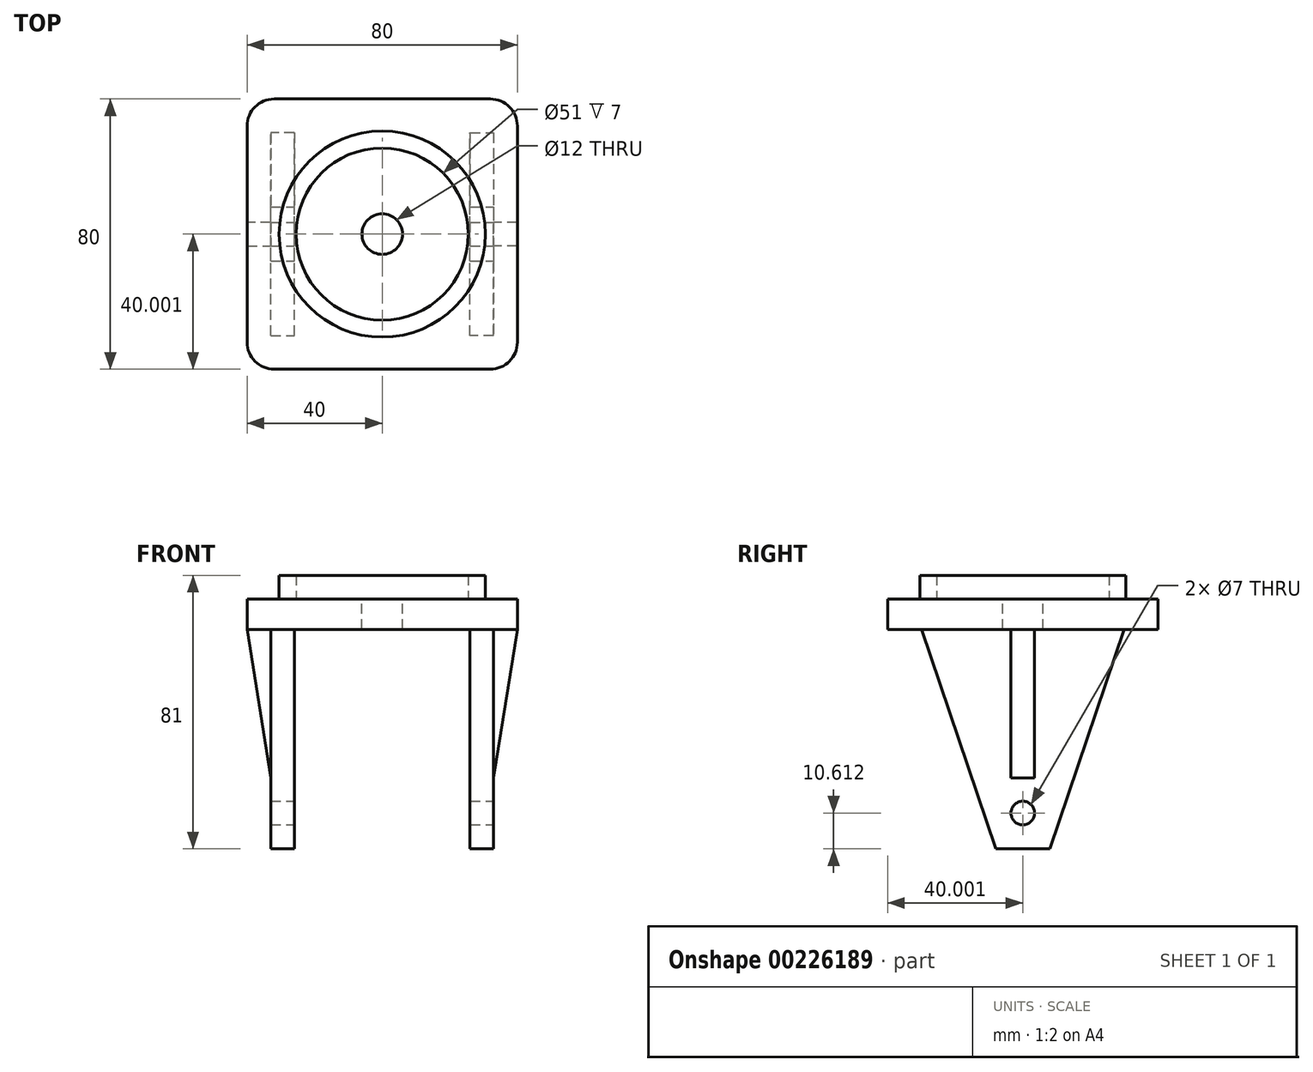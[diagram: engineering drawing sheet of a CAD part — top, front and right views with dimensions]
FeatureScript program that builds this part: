
annotation { "Feature Type Name" : "Feature", "Feature Type Description" : "" }
export const myFeature = defineFeature(function(context is Context, id is Id, definition is map)
    precondition{}
    {
        {
            var Q0;
            Q0=qCreatedBy(makeId("Top.planeOp"),FACE);
            var sketch = newSketch(context, id + "F0", { "sketchPlane" : qUnion([Q0])});
            skLineSegment(sketch, "E0.bottom", {"start": v(-30.4, 30.32) * mm, "end": v(33.6, 30.32) * mm});
            skLineSegment(sketch, "E0.top", {"start": v(-30.4, -49.68) * mm, "end": v(33.6, -49.68) * mm});
            skLineSegment(sketch, "E0.left", {"start": v(-38.4, 22.32) * mm, "end": v(-38.4, -41.68) * mm});
            skLineSegment(sketch, "E0.right", {"start": v(41.6, 22.32) * mm, "end": v(41.6, -41.68) * mm});
            skPoint(sketch, "E1.visualSharp", {"position": v(-38.4, 30.32) * mm});
            skArc(sketch, "E1.filletArc", {"start": v(-30.4, 30.32) * mm, "mid": v(-36.05, 27.98) * mm, "end": v(-38.4, 22.32) * mm});
            skPoint(sketch, "E2.visualSharp", {"position": v(41.6, 30.32) * mm});
            skArc(sketch, "E2.filletArc", {"start": v(41.6, 22.32) * mm, "mid": v(39.27, 27.98) * mm, "end": v(33.6, 30.32) * mm});
            skPoint(sketch, "E3.visualSharp", {"position": v(41.6, -49.68) * mm});
            skArc(sketch, "E3.filletArc", {"start": v(33.6, -49.68) * mm, "mid": v(39.27, -47.34) * mm, "end": v(41.6, -41.68) * mm});
            skPoint(sketch, "E4.visualSharp", {"position": v(-38.4, -49.68) * mm});
            skArc(sketch, "E4.filletArc", {"start": v(-38.4, -41.68) * mm, "mid": v(-36.05, -47.34) * mm, "end": v(-30.4, -49.68) * mm});
            skSolve(sketch);
        }
        {
            var Q0;
            Q0 = qSketchRegion(id + "F0", true);
            extrude(context, id + "F1", {"entities" : qUnion([Q0]), "depth" : 9 * mm});
        }
        {
            var Q0;
            Q0=makeQuery(id+"F1.opExtrude","CAP_FACE",FACE,{"disambiguationData":[OSD([sQuery(id+"F0.wireOp",EDGE,"E0.bottom"),sQuery(id+"F0.wireOp",EDGE,"E0.top"),sQuery(id+"F0.wireOp",EDGE,"E0.left"),sQuery(id+"F0.wireOp",EDGE,"E0.right"),sQuery(id+"F0.wireOp",EDGE,"E1.filletArc"),sQuery(id+"F0.wireOp",EDGE,"E2.filletArc"),sQuery(id+"F0.wireOp",EDGE,"E3.filletArc"),sQuery(id+"F0.wireOp",EDGE,"E4.filletArc")])],"isStart":false});
            var sketch = newSketch(context, id + "F2", { "sketchPlane" : qUnion([Q0])});
            skCircle(sketch, "E5", {"center": v(1.6, -9.68) * mm, "radius": 30.5 * mm});
            skPoint(sketch, "E5.centerSnap0", {"position": v(-38.4, -9.68) * mm});
            skPoint(sketch, "E5.centerSnap1", {"position": v(1.6, 30.32) * mm});
            skCircle(sketch, "E6", {"center": v(1.6, -9.68) * mm, "radius": 25.5 * mm});
            skSolve(sketch);
        }
        {
            var Q0;
            Q0=makeQuery(id+"F2.imprint","IMPRINT",FACE,{"disambiguationData":[TD([[makeQuery(id+"F2.imprint","IMPRINT",EDGE,{"derivedFrom":sQuery(id+"F2.wireOp",EDGE,"E5")}),1.0]])]});
            extrude(context, id + "F3", {"entities" : qUnion([Q0]), "operationType" : NewBodyOperationType.ADD, "depth" : 7 * mm});
        }
        {
            var Q0;
            {var subQ0=sQuery(id+"F0.wireOp",EDGE,"E0.right");var subQ1=sQuery(id+"F0.wireOp",EDGE,"E0.left");var subQ2=sQuery(id+"F0.wireOp",EDGE,"E0.top");var subQ3=sQuery(id+"F0.wireOp",EDGE,"E0.bottom");var subQ4=sQuery(id+"F0.wireOp",EDGE,"E1.filletArc");var subQ5=sQuery(id+"F0.wireOp",EDGE,"E2.filletArc");var subQ6=sQuery(id+"F0.wireOp",EDGE,"E3.filletArc");var subQ7=sQuery(id+"F0.wireOp",EDGE,"E4.filletArc");Q0=makeQuery(id+"F3.boolean.opBoolean","SPLIT",FACE,{"disambiguationData":[TD([makeQuery(id+"F1.opExtrude","SWEPT_FACE",FACE,{"disambiguationData":[OSD([subQ3])]})])],"derivedFrom":makeQuery(id+"F1.opExtrude","CAP_FACE",FACE,{"disambiguationData":[OSD([subQ3,subQ2,subQ1,subQ0,subQ4,subQ5,subQ6,subQ7])],"isStart":false})});}
            var sketch = newSketch(context, id + "F4", { "sketchPlane" : qUnion([Q0])});
            skCircle(sketch, "E7", {"center": v(1.6, -9.68) * mm, "radius": 6 * mm});
            skSolve(sketch);
        }
        {
            var Q0;
            Q0=makeQuery(id+"F4.imprint","IMPRINT",FACE,{"disambiguationData":[TD([[makeQuery(id+"F4.imprint","IMPRINT",EDGE,{"derivedFrom":sQuery(id+"F4.wireOp",EDGE,"E7")}),1.0]])]});
            extrude(context, id + "F5", {"entities" : qUnion([Q0]), "operationType" : NewBodyOperationType.REMOVE, "endBound" : BoundingType.THROUGH_ALL, "oppositeDirection" : true, "depth" : 25 * mm});
        }
        {
            var Q0;
            Q0=makeQuery(id+"F1.opExtrude","CAP_FACE",FACE,{"disambiguationData":[OSD([sQuery(id+"F0.wireOp",EDGE,"E0.bottom"),sQuery(id+"F0.wireOp",EDGE,"E0.top"),sQuery(id+"F0.wireOp",EDGE,"E0.left"),sQuery(id+"F0.wireOp",EDGE,"E0.right"),sQuery(id+"F0.wireOp",EDGE,"E1.filletArc"),sQuery(id+"F0.wireOp",EDGE,"E2.filletArc"),sQuery(id+"F0.wireOp",EDGE,"E3.filletArc"),sQuery(id+"F0.wireOp",EDGE,"E4.filletArc")])],"isStart":true});
            var sketch = newSketch(context, id + "F6", { "sketchPlane" : qUnion([Q0])});
            skLineSegment(sketch, "E8", {"start": v(-31.4, 39.68) * mm, "end": v(-31.4, -20.32) * mm});
            skLineSegment(sketch, "E9", {"start": v(-31.4, 39.68) * mm, "end": v(-24.4, 39.68) * mm});
            skLineSegment(sketch, "E10", {"start": v(-24.4, 39.68) * mm, "end": v(-24.4, -20.32) * mm});
            skLineSegment(sketch, "E11", {"start": v(-24.4, -20.32) * mm, "end": v(-31.4, -20.32) * mm});
            skLineSegment(sketch, "E12", {"start": v(27.6, 39.68) * mm, "end": v(27.6, -20.32) * mm});
            skLineSegment(sketch, "E13", {"start": v(27.6, -20.32) * mm, "end": v(34.6, -20.32) * mm});
            skLineSegment(sketch, "E14", {"start": v(34.6, -20.32) * mm, "end": v(34.6, 39.68) * mm});
            skLineSegment(sketch, "E15", {"start": v(34.6, 39.68) * mm, "end": v(27.6, 39.68) * mm});
            skSolve(sketch);
        }
        {
            var Q0;
            Q0=makeQuery(id+"F6.imprint","IMPRINT",FACE,{"disambiguationData":[TD([[makeQuery(id+"F6.imprint","IMPRINT",EDGE,{"derivedFrom":sQuery(id+"F6.wireOp",EDGE,"E8")}),1.0]])]});
            var Q1;
            Q1=makeQuery(id+"F6.imprint","IMPRINT",FACE,{"disambiguationData":[TD([[makeQuery(id+"F6.imprint","IMPRINT",EDGE,{"derivedFrom":sQuery(id+"F6.wireOp",EDGE,"E12")}),1.0]])]});
            extrude(context, id + "F7", {"entities" : qUnion([Q0, Q1]), "operationType" : NewBodyOperationType.ADD, "depth" : 65 * mm});
        }
        {
            var Q0;
            Q0=makeQuery(id+"F7.opExtrude","SWEPT_FACE",FACE,{"disambiguationData":[OSD([sQuery(id+"F6.wireOp",EDGE,"E14")])]});
            var sketch = newSketch(context, id + "F8", { "sketchPlane" : qUnion([Q0])});
            skLineSegment(sketch, "E16", {"start": v(20.32, 0) * mm, "end": v(-1.68, -65) * mm});
            skLineSegment(sketch, "E17", {"start": v(-39.68, 0) * mm, "end": v(-17.68, -65) * mm});
            skLineSegment(sketch, "E18", {"start": v(-17.68, -65) * mm, "end": v(-39.68, -65) * mm});
            skLineSegment(sketch, "E19", {"start": v(-39.68, -65) * mm, "end": v(-39.68, 0) * mm});
            skLineSegment(sketch, "E20", {"start": v(20.32, 0) * mm, "end": v(20.32, -65) * mm});
            skLineSegment(sketch, "E21", {"start": v(20.32, -65) * mm, "end": v(-1.68, -65) * mm});
            skSolve(sketch);
        }
        {
            var Q0;
            Q0 = qSketchRegion(id + "F8", true);
            extrude(context, id + "F9", {"entities" : qUnion([Q0]), "operationType" : NewBodyOperationType.REMOVE, "endBound" : BoundingType.THROUGH_ALL, "oppositeDirection" : true, "depth" : 25 * mm});
        }
        {
            var Q0;
            Q0=makeQuery(id+"F7.opExtrude","SWEPT_FACE",FACE,{"disambiguationData":[OSD([sQuery(id+"F6.wireOp",EDGE,"E14")])]});
            var sketch = newSketch(context, id + "F10", { "sketchPlane" : qUnion([Q0])});
            skLineSegment(sketch, "E22", {"start": v(-9.68, 0) * mm, "end": v(-6.18, 0) * mm});
            skLineSegment(sketch, "E23", {"start": v(-6.18, 0) * mm, "end": v(-6.18, -44) * mm});
            skLineSegment(sketch, "E24", {"start": v(-6.18, -44) * mm, "end": v(-13.18, -44) * mm});
            skLineSegment(sketch, "E25", {"start": v(-13.18, -44) * mm, "end": v(-13.18, 0) * mm});
            skLineSegment(sketch, "E26", {"start": v(-13.18, 0) * mm, "end": v(-9.68, 0) * mm});
            skSolve(sketch);
        }
        {
            var Q0;
            Q0=makeQuery(id+"F10.imprint","IMPRINT",FACE,{"disambiguationData":[TD([[makeQuery(id+"F10.imprint","IMPRINT",EDGE,{"derivedFrom":sQuery(id+"F10.wireOp",EDGE,"E22")}),1.0]])]});
            extrude(context, id + "F11", {"entities" : qUnion([Q0]), "operationType" : NewBodyOperationType.ADD, "depth" : 7 * mm});
        }
        {
            var Q0;
            Q0=makeQuery(id+"F11.opExtrude","SWEPT_FACE",FACE,{"disambiguationData":[OSD([sQuery(id+"F10.wireOp",EDGE,"E23")])]});
            var sketch = newSketch(context, id + "F12", { "sketchPlane" : qUnion([Q0])});
            skLineSegment(sketch, "E27", {"start": v(-41.6, 0) * mm, "end": v(-34.6, -44) * mm});
            skLineSegment(sketch, "E28", {"start": v(-34.6, -44) * mm, "end": v(-41.6, -44) * mm});
            skLineSegment(sketch, "E29", {"start": v(-41.6, -44) * mm, "end": v(-41.6, 0) * mm});
            skSolve(sketch);
        }
        {
            var Q0;
            Q0 = qSketchRegion(id + "F12", true);
            extrude(context, id + "F13", {"entities" : qUnion([Q0]), "operationType" : NewBodyOperationType.REMOVE, "endBound" : BoundingType.THROUGH_ALL, "oppositeDirection" : true, "depth" : 25 * mm});
        }
        {
            var Q0;
            Q0=makeQuery(id+"F7.opExtrude","SWEPT_FACE",FACE,{"disambiguationData":[OSD([sQuery(id+"F6.wireOp",EDGE,"E8")])]});
            var sketch = newSketch(context, id + "F14", { "sketchPlane" : qUnion([Q0])});
            skLineSegment(sketch, "E30", {"start": v(9.68, 0) * mm, "end": v(13.18, 0) * mm});
            skLineSegment(sketch, "E31", {"start": v(13.18, 0) * mm, "end": v(13.18, -44) * mm});
            skLineSegment(sketch, "E32", {"start": v(13.18, -44) * mm, "end": v(6.18, -44) * mm});
            skLineSegment(sketch, "E33", {"start": v(6.18, -44) * mm, "end": v(6.18, 0) * mm});
            skLineSegment(sketch, "E34", {"start": v(6.18, 0) * mm, "end": v(9.68, 0) * mm});
            skSolve(sketch);
        }
        {
            var Q0;
            Q0 = qSketchRegion(id + "F14", true);
            extrude(context, id + "F15", {"entities" : qUnion([Q0]), "operationType" : NewBodyOperationType.ADD, "depth" : 7 * mm});
        }
        {
            var Q0;
            Q0=makeQuery(id+"F15.opExtrude","SWEPT_FACE",FACE,{"disambiguationData":[OSD([sQuery(id+"F14.wireOp",EDGE,"E31")])]});
            var sketch = newSketch(context, id + "F16", { "sketchPlane" : qUnion([Q0])});
            skLineSegment(sketch, "E35", {"start": v(-38.4, 0) * mm, "end": v(-31.4, -44) * mm});
            skLineSegment(sketch, "E36", {"start": v(-31.4, -44) * mm, "end": v(-38.4, -44) * mm});
            skLineSegment(sketch, "E37", {"start": v(-38.4, -44) * mm, "end": v(-38.4, 0) * mm});
            skSolve(sketch);
        }
        {
            var Q0;
            Q0 = qSketchRegion(id + "F16", true);
            extrude(context, id + "F17", {"entities" : qUnion([Q0]), "operationType" : NewBodyOperationType.REMOVE, "endBound" : BoundingType.THROUGH_ALL, "oppositeDirection" : true, "depth" : 25 * mm});
        }
        {
            var Q0;
            Q0=makeQuery(id+"F7.opExtrude","SWEPT_FACE",FACE,{"disambiguationData":[OSD([sQuery(id+"F6.wireOp",EDGE,"E14")])]});
            var sketch = newSketch(context, id + "F18", { "sketchPlane" : qUnion([Q0])});
            skLineSegment(sketch, "E38", {"start": v(-6.18, 0) * mm, "end": v(-9.68, 0) * mm});
            skCircle(sketch, "E39", {"center": v(-9.68, -54.39) * mm, "radius": 3.5 * mm});
            skSolve(sketch);
        }
        {
            var Q0;
            Q0=makeQuery(id+"F18.imprint","IMPRINT",FACE,{"disambiguationData":[TD([[makeQuery(id+"F18.imprint","IMPRINT",EDGE,{"derivedFrom":sQuery(id+"F18.wireOp",EDGE,"E39")}),1.0]])]});
            extrude(context, id + "F19", {"entities" : qUnion([Q0]), "operationType" : NewBodyOperationType.REMOVE, "endBound" : BoundingType.THROUGH_ALL, "oppositeDirection" : true, "depth" : 25 * mm});
        }
    });
